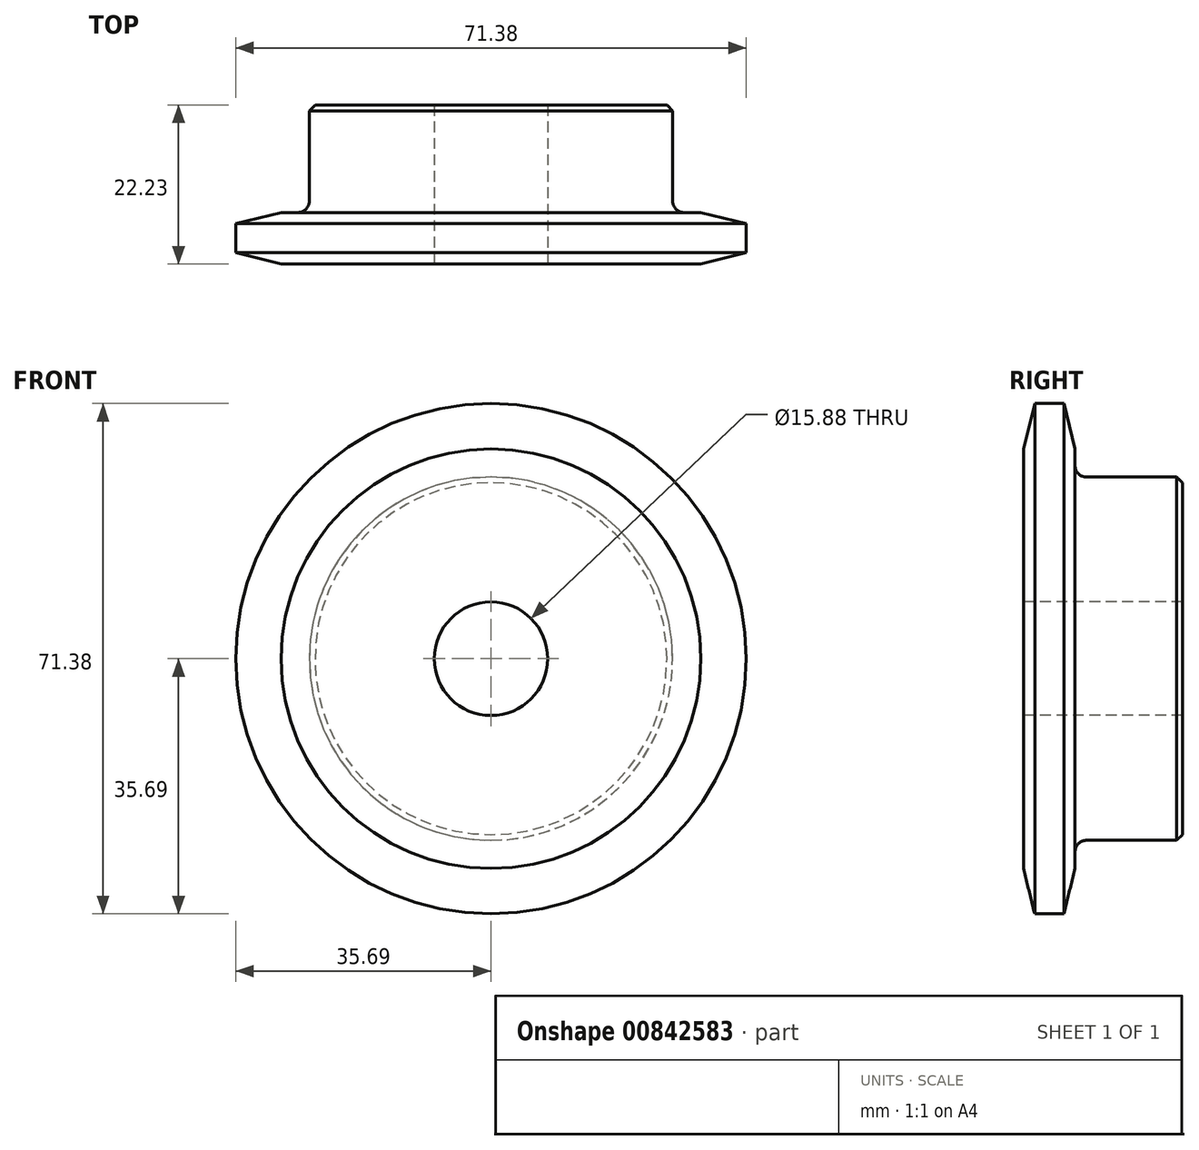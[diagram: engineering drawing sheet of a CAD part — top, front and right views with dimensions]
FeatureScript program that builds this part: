
annotation { "Feature Type Name" : "Feature", "Feature Type Description" : "" }
export const myFeature = defineFeature(function(context is Context, id is Id, definition is map)
    precondition{}
    {
        {
            var Q0;
            Q0=qCreatedBy(makeId("Right.planeOp"),FACE);
            var sketch = newSketch(context, id + "F0", { "sketchPlane" : qUnion([Q0])});
            skLineSegment(sketch, "E0", {"start": v(0, 0) * mm, "end": v(35.72, 0) * mm, "construction": true});
            skLineSegment(sketch, "E1.bottom", {"start": v(0, 7.94) * mm, "end": v(7.21, 7.94) * mm});
            skLineSegment(sketch, "E1.top", {"start": v(0, 35.69) * mm, "end": v(7.21, 35.69) * mm});
            skLineSegment(sketch, "E1.left", {"start": v(0, 7.94) * mm, "end": v(0, 35.69) * mm});
            skLineSegment(sketch, "E1.right", {"start": v(7.21, 7.94) * mm, "end": v(7.21, 35.69) * mm});
            skLineSegment(sketch, "E2.bottom", {"start": v(0, 25.4) * mm, "end": v(22.23, 25.4) * mm});
            skLineSegment(sketch, "E2.top", {"start": v(0, 7.94) * mm, "end": v(22.23, 7.94) * mm});
            skLineSegment(sketch, "E2.left", {"start": v(0, 25.4) * mm, "end": v(0, 7.94) * mm});
            skLineSegment(sketch, "E2.right", {"start": v(22.23, 25.4) * mm, "end": v(22.23, 7.94) * mm});
            skLineSegment(sketch, "E3.MirrorCS", {"start": v(22.23, -25.4) * mm, "end": v(22.23, -7.94) * mm});
            skLineSegment(sketch, "E4.MirrorCS", {"start": v(0, -25.4) * mm, "end": v(22.23, -25.4) * mm});
            skLineSegment(sketch, "E5.MirrorCS", {"start": v(0, -7.94) * mm, "end": v(7.21, -7.94) * mm});
            skLineSegment(sketch, "E6.MirrorCS", {"start": v(0, -25.4) * mm, "end": v(0, -7.94) * mm});
            skLineSegment(sketch, "E7.MirrorCS", {"start": v(0, -7.94) * mm, "end": v(22.23, -7.94) * mm});
            skLineSegment(sketch, "E8.MirrorCS", {"start": v(0, -7.94) * mm, "end": v(0, -35.69) * mm});
            skLineSegment(sketch, "E9.MirrorCS", {"start": v(0, -35.69) * mm, "end": v(7.21, -35.69) * mm});
            skLineSegment(sketch, "E10.MirrorCS", {"start": v(7.21, -7.94) * mm, "end": v(7.21, -35.69) * mm});
            skSolve(sketch);
        }
        {
            var Q0;
            {var subQ0=sQuery(id+"F0.wireOp",EDGE,"E2.top");Q0=makeQuery(id+"F0.imprint","IMPRINT",FACE,{"disambiguationData":[TD([[makeQuery(id+"F0.imprint","IMPRINT",EDGE,{"derivedFrom":subQ0}),1.0]])]});}
            var Q1;
            {var subQ0=sQuery(id+"F0.wireOp",EDGE,"E1.bottom");Q1=makeQuery(id+"F0.imprint","IMPRINT",FACE,{"disambiguationData":[TD([[makeQuery(id+"F0.imprint","IMPRINT",EDGE,{"derivedFrom":subQ0}),1.0]])]});}
            var Q2;
            {var subQ0=sQuery(id+"F0.wireOp",EDGE,"E1.top");Q2=makeQuery(id+"F0.imprint","IMPRINT",FACE,{"disambiguationData":[TD([[makeQuery(id+"F0.imprint","IMPRINT",EDGE,{"derivedFrom":subQ0}),-1.0]])]});}
            var Q3;
            Q3=sQuery(id+"F0.wireOp",EDGE,"E0");
            revolve(context, id + "F1", {"surfaceOperationType" : NewSurfaceOperationType.NEW, "entities" : qUnion([Q0, Q1, Q2]), "axis" : qUnion([Q3]), "revolveType" : RevolveType.FULL});
        }
        {
            var Q0;
            Q0=makeQuery(id+"F1.opRevolve","SWEPT_EDGE",EDGE,{"disambiguationData":[OSD([sQuery(id+"F0.wireOp",EDGE,"E1.right"),sQuery(id+"F0.wireOp",EDGE,"E2.bottom")])]});
            fillet(context, id + "F2", {"entities" : qUnion([Q0]), "radius" : 1.6 * mm, "tangentPropagation" : true, "allowEdgeOverflow" : false});
        }
        {
            var Q0;
            Q0=makeQuery(id+"F1.opRevolve","SWEPT_EDGE",EDGE,{"disambiguationData":[OSD([sQuery(id+"F0.wireOp",EDGE,"E2.bottom"),sQuery(id+"F0.wireOp",EDGE,"E2.right")])]});
            chamfer(context, id + "F3", {"entities" : qUnion([Q0]), "width" : 0.8 * mm, "tangentPropagation" : true});
        }
        {
            var Q0;
            Q0=makeQuery(id+"F1.opRevolve","SWEPT_EDGE",EDGE,{"disambiguationData":[OSD([sQuery(id+"F0.wireOp",EDGE,"E1.top"),sQuery(id+"F0.wireOp",EDGE,"E1.left")])]});
            var Q1;
            Q1=makeQuery(id+"F1.opRevolve","SWEPT_EDGE",EDGE,{"disambiguationData":[OSD([sQuery(id+"F0.wireOp",EDGE,"E1.top"),sQuery(id+"F0.wireOp",EDGE,"E1.right")])]});
            chamfer(context, id + "F4", {"entities" : qUnion([Q0, Q1]), "chamferType" : ChamferType.TWO_OFFSETS, "width1" : 6.35 * mm, "oppositeDirection" : false, "width2" : 1.57 * mm, "tangentPropagation" : true});
        }
    });
